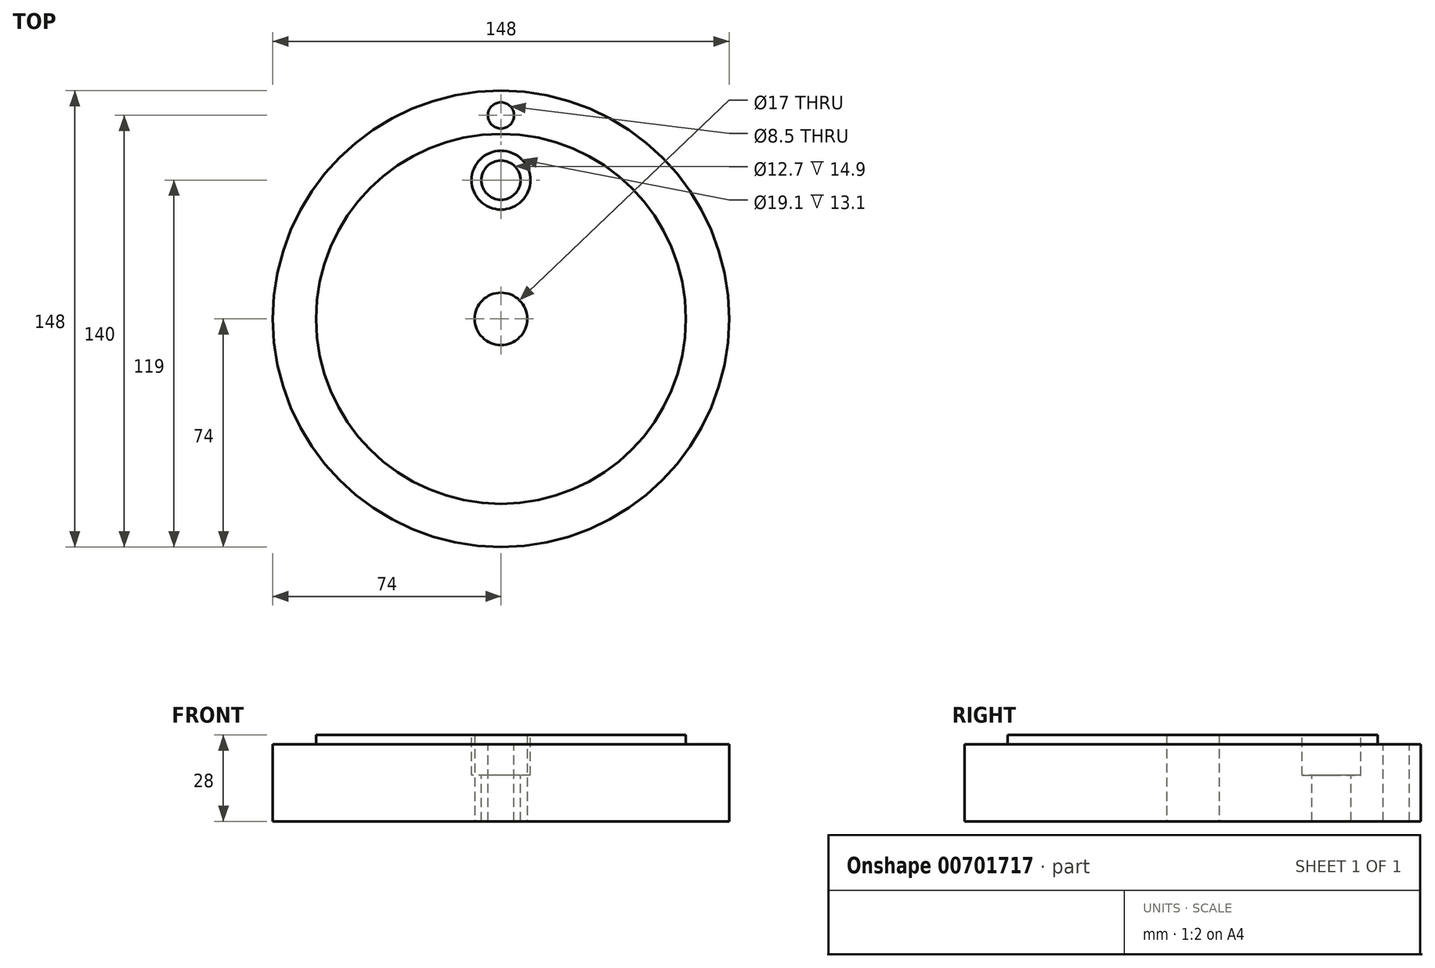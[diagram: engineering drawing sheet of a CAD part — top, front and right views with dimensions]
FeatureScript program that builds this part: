
annotation { "Feature Type Name" : "Feature", "Feature Type Description" : "" }
export const myFeature = defineFeature(function(context is Context, id is Id, definition is map)
    precondition{}
    {
        {
            var Q0;
            Q0=qCreatedBy(makeId("Top.planeOp"),FACE);
            var sketch = newSketch(context, id + "F0", { "sketchPlane" : qUnion([Q0])});
            skCircle(sketch, "E0", {"center": v(0, 0) * mm, "radius": 74 * mm});
            skSolve(sketch);
        }
        {
            var Q0;
            Q0=makeQuery(id+"F0.imprint","IMPRINT",FACE,{"disambiguationData":[TD([[makeQuery(id+"F0.imprint","IMPRINT",EDGE,{"derivedFrom":sQuery(id+"F0.wireOp",EDGE,"E0")}),1.0]])]});
            extrude(context, id + "F1", {"entities" : qUnion([Q0]), "depth" : 25 * mm, "offsetDistance" : 25 * mm});
        }
        {
            var Q0;
            Q0=makeQuery(id+"F1.opExtrude","CAP_FACE",FACE,{"disambiguationData":[OSD([sQuery(id+"F0.wireOp",EDGE,"E0")])],"isStart":false});
            var sketch = newSketch(context, id + "F2", { "sketchPlane" : qUnion([Q0])});
            skCircle(sketch, "E1", {"center": v(0, 0) * mm, "radius": 60 * mm});
            skSolve(sketch);
        }
        {
            var Q0;
            Q0=makeQuery(id+"F2.imprint","IMPRINT",FACE,{"disambiguationData":[TD([[makeQuery(id+"F2.imprint","IMPRINT",EDGE,{"derivedFrom":sQuery(id+"F2.wireOp",EDGE,"E1")}),1.0]])]});
            extrude(context, id + "F3", {"entities" : qUnion([Q0]), "operationType" : NewBodyOperationType.ADD, "depth" : 3 * mm, "offsetDistance" : 25 * mm});
        }
        {
            var Q0;
            Q0=sQuery(id+"F0.wireOp",VERTEX,"E0.center");
            var Q1;
            Q1=makeQuery(id+"F1.opExtrude","SWEPT_BODY",BODY,{"disambiguationData":[OSD([sQuery(id+"F0.wireOp",EDGE,"E0")])]});
            hole(context, id + "F4", {"style" : HoleStyle.SIMPLE, "endStyle" : HoleEndStyle.THROUGH, "oppositeDirection" : true, "holeDiameter" : 17 * mm, "majorDiameter" : 5 * mm, "isTappedThrough" : true, "tappedDepth" : 12 * mm, "tapClearance" : 3, "startFromSketch" : true, "locations" : qUnion([Q0]), "scope" : qUnion([Q1])});
        }
        {
            var Q0;
            Q0=makeQuery(id+"F1.opExtrude","CAP_FACE",FACE,{"disambiguationData":[OSD([sQuery(id+"F0.wireOp",EDGE,"E0")])],"isStart":false});
            var sketch = newSketch(context, id + "F5", { "sketchPlane" : qUnion([Q0])});
            skCircle(sketch, "E2", {"center": v(0, 0) * mm, "radius": 66 * mm, "construction": true});
            skPoint(sketch, "E3", {"position": v(0, 66) * mm});
            skSolve(sketch);
        }
        {
            var Q0;
            Q0=sQuery(id+"F5.wireOp",VERTEX,"E3");
            var Q1;
            Q1=makeQuery(id+"F1.opExtrude","SWEPT_BODY",BODY,{"disambiguationData":[OSD([sQuery(id+"F0.wireOp",EDGE,"E0")])]});
            hole(context, id + "F6", {"style" : HoleStyle.SIMPLE, "endStyle" : HoleEndStyle.THROUGH, "holeDiameter" : 8.5 * mm, "majorDiameter" : 5 * mm, "isTappedThrough" : true, "tappedDepth" : 12 * mm, "tapClearance" : 3, "startFromSketch" : true, "locations" : qUnion([Q0]), "scope" : qUnion([Q1])});
        }
        {
            var Q0;
            Q0=makeQuery(id+"F3.opExtrude","CAP_FACE",FACE,{"disambiguationData":[OSD([sQuery(id+"F2.wireOp",EDGE,"E1")])],"isStart":false});
            var sketch = newSketch(context, id + "F7", { "sketchPlane" : qUnion([Q0])});
            skCircle(sketch, "E4", {"center": v(0, 0) * mm, "radius": 45 * mm, "construction": true});
            skPoint(sketch, "E5", {"position": v(0, 45) * mm});
            skSolve(sketch);
        }
        {
            var Q0;
            Q0=sQuery(id+"F7.wireOp",VERTEX,"E5");
            var Q1;
            Q1=makeQuery(id+"F1.opExtrude","SWEPT_BODY",BODY,{"disambiguationData":[OSD([sQuery(id+"F0.wireOp",EDGE,"E0")])]});
            hole(context, id + "F8", {"style" : HoleStyle.C_BORE, "endStyle" : HoleEndStyle.THROUGH, "holeDiameter" : 12.7 * mm, "cBoreDiameter" : 19.1 * mm, "cBoreDepth" : 13.1 * mm, "majorDiameter" : 5 * mm, "isTappedThrough" : true, "tappedDepth" : 12 * mm, "tapClearance" : 3, "startFromSketch" : true, "locations" : qUnion([Q0]), "scope" : qUnion([Q1])});
        }
    });
